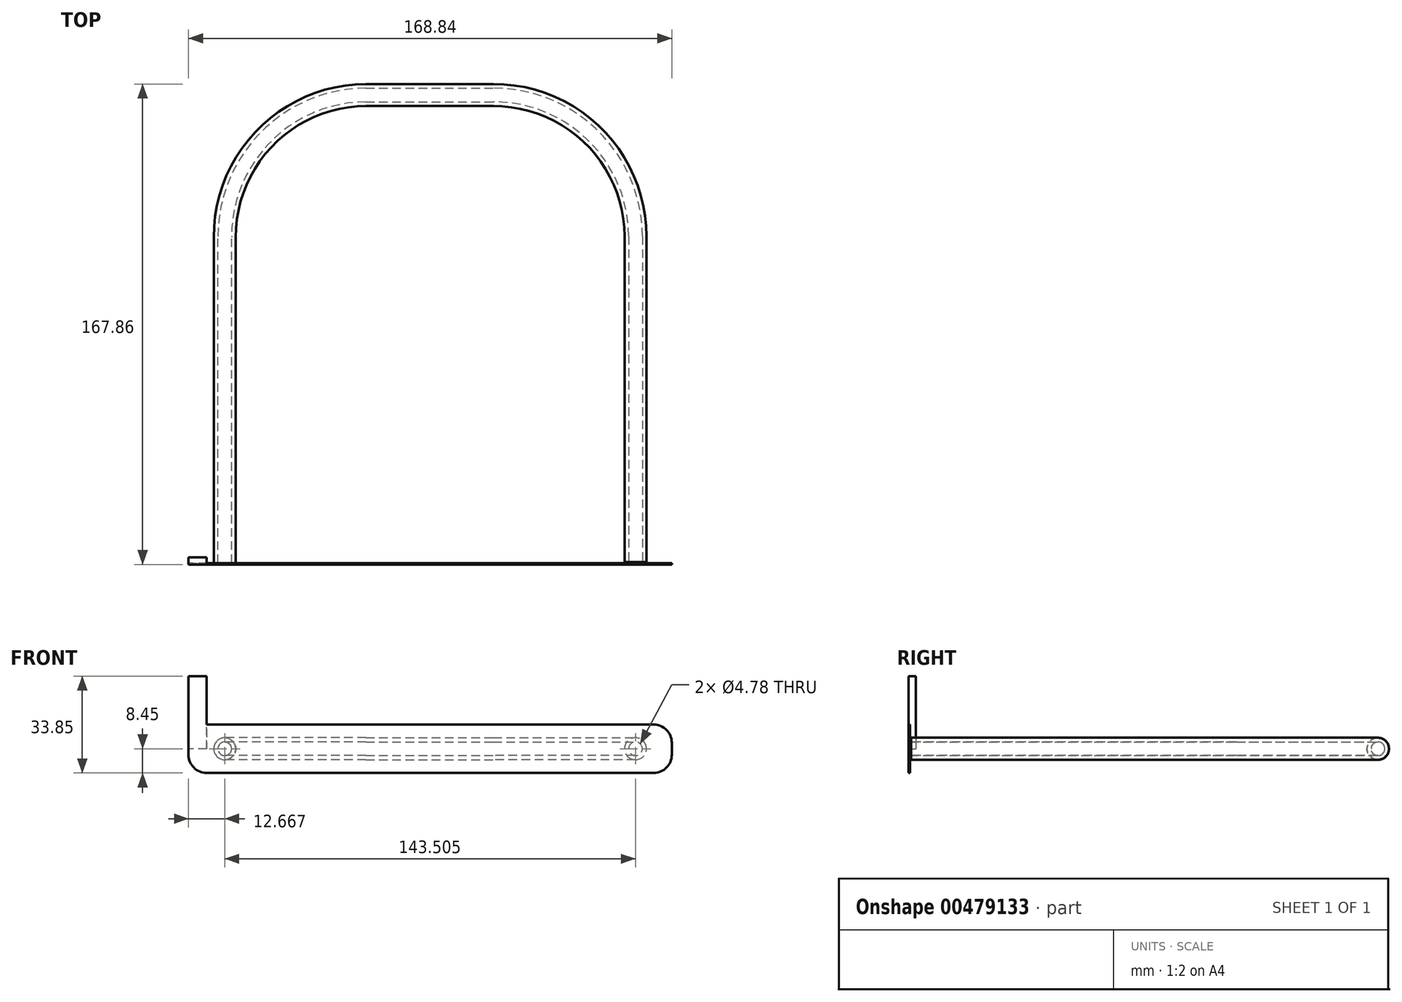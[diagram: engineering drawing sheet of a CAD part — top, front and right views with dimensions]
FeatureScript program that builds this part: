
annotation { "Feature Type Name" : "Feature", "Feature Type Description" : "" }
export const myFeature = defineFeature(function(context is Context, id is Id, definition is map)
    precondition{}
    {
        {
            var Q0;
            Q0=qCreatedBy(makeId("Top.planeOp"),FACE);
            var sketch = newSketch(context, id + "F0", { "sketchPlane" : qUnion([Q0])});
            skLineSegment(sketch, "E0", {"start": v(-71.78, -34.1) * mm, "end": v(-71.78, 79.72) * mm});
            skArc(sketch, "E1", {"start": v(-22.25, 129.26) * mm, "mid": v(-57.28, 114.75) * mm, "end": v(-71.78, 79.72) * mm});
            skArc(sketch, "E2.MirrorCS", {"start": v(22.25, 129.26) * mm, "mid": v(57.28, 114.75) * mm, "end": v(71.78, 79.72) * mm});
            skLineSegment(sketch, "E3.MirrorCS", {"start": v(71.78, -34.1) * mm, "end": v(71.78, 79.72) * mm});
            skLineSegment(sketch, "E4", {"start": v(-22.25, 129.26) * mm, "end": v(22.25, 129.26) * mm});
            skSolve(sketch);
        }
        {
            var Q0;
            Q0=qCreatedBy(makeId("Front.planeOp"),FACE);
            cPlane(context, id + "F1", {"entities" : qUnion([Q0]), "cplaneType" : CPlaneType.OFFSET, "offset" : 34.3 * mm, "width" : 152.4 * mm, "height" : 152.4 * mm});
        }
        {
            var Q0;
            Q0=qCreatedBy(id+"F1.planeOp",FACE);
            var sketch = newSketch(context, id + "F2", { "sketchPlane" : qUnion([Q0])});
            skCircle(sketch, "E5", {"center": v(-71.75, 0) * mm, "radius": 3.84 * mm});
            skCircle(sketch, "E6", {"center": v(-71.75, 0) * mm, "radius": 2.39 * mm});
            skSolve(sketch);
        }
        {
            var Q0;
            Q0=makeQuery(id+"F2.imprint","IMPRINT",FACE,{"disambiguationData":[TD([[makeQuery(id+"F2.imprint","IMPRINT",EDGE,{"derivedFrom":sQuery(id+"F2.wireOp",EDGE,"E5")}),1.0]])]});
            var Q1;
            Q1=sQuery(id+"F0.wireOp",EDGE,"E0");
            var Q2;
            Q2=sQuery(id+"F0.wireOp",EDGE,"E4");
            var Q3;
            Q3=sQuery(id+"F0.wireOp",EDGE,"E1");
            var Q4;
            Q4=sQuery(id+"F0.wireOp",EDGE,"E2.MirrorCS");
            var Q5;
            Q5=sQuery(id+"F0.wireOp",EDGE,"E3.MirrorCS");
            sweep(context, id + "F3", {"profiles" : qUnion([Q0]), "path" : qUnion([Q1, Q2, Q3, Q4, Q5])});
        }
        {
            var Q0;
            Q0=qCreatedBy(id+"F1.planeOp",FACE);
            var sketch = newSketch(context, id + "F4", { "sketchPlane" : qUnion([Q0])});
            skLineSegment(sketch, "E7", {"start": v(61.37, 0) * mm, "end": v(78.27, 0) * mm, "construction": true});
            skLineSegment(sketch, "E8", {"start": v(78.27, 8.45) * mm, "end": v(-78.07, 8.45) * mm});
            skLineSegment(sketch, "E9.MirrorCS", {"start": v(78.27, -8.45) * mm, "end": v(-78.07, -8.45) * mm});
            skLineSegment(sketch, "E10", {"start": v(-84.42, -2.1) * mm, "end": v(-84.42, 2.1) * mm});
            skArc(sketch, "E11.filletArc", {"start": v(-78.07, 8.45) * mm, "mid": v(-82.56, 6.6) * mm, "end": v(-84.42, 2.1) * mm});
            skArc(sketch, "E12.filletArc", {"start": v(-84.42, -2.1) * mm, "mid": v(-82.56, -6.6) * mm, "end": v(-78.07, -8.45) * mm});
            skLineSegment(sketch, "E13", {"start": v(0, 0) * mm, "end": v(0, 47.43) * mm, "construction": true});
            skArc(sketch, "E14.MirrorCS", {"start": v(78.07, 8.45) * mm, "mid": v(82.56, 6.6) * mm, "end": v(84.42, 2.1) * mm});
            skArc(sketch, "E15.MirrorCS", {"start": v(84.42, -2.1) * mm, "mid": v(82.56, -6.6) * mm, "end": v(78.07, -8.45) * mm});
            skLineSegment(sketch, "E16.MirrorCS", {"start": v(84.42, -2.1) * mm, "end": v(84.42, 2.1) * mm});
            skSolve(sketch);
        }
        {
            var Q0;
            Q0 = qSketchRegion(id + "F4", true);
            extrude(context, id + "F5", {"entities" : qUnion([Q0]), "depth" : .5 * mm, "offsetDistance" : 25.4 * mm});
        }
        {
            var Q0;
            Q0=qCreatedBy(makeId("Top.planeOp"),FACE);
            var sketch = newSketch(context, id + "F6", { "sketchPlane" : qUnion([Q0])});
            skLineSegment(sketch, "E17.0", {"start": v(-78.07, -34.8) * mm, "end": v(-84.42, -34.8) * mm});
            skLineSegment(sketch, "E18.0", {"start": v(78.07, -34.8) * mm, "end": v(-78.07, -34.8) * mm});
            skLineSegment(sketch, "E19.0", {"start": v(-78.07, -32.25) * mm, "end": v(-84.42, -32.25) * mm});
            skLineSegment(sketch, "E20", {"start": v(-78.07, -32.25) * mm, "end": v(-78.07, -34.8) * mm});
            skLineSegment(sketch, "E21", {"start": v(-84.42, -34.8) * mm, "end": v(-84.42, -32.25) * mm});
            skSolve(sketch);
        }
        {
            var Q0;
            Q0=makeQuery(id+"F6.imprint","IMPRINT",FACE,{"disambiguationData":[TD([[makeQuery(id+"F6.imprint","IMPRINT",EDGE,{"derivedFrom":sQuery(id+"F6.wireOp",EDGE,"E17.0")}),-1.0]])]});
            extrude(context, id + "F7", {"entities" : qUnion([Q0]), "operationType" : NewBodyOperationType.ADD, "depth" : 25.4 * mm, "offsetDistance" : 25.4 * mm});
        }
    });
